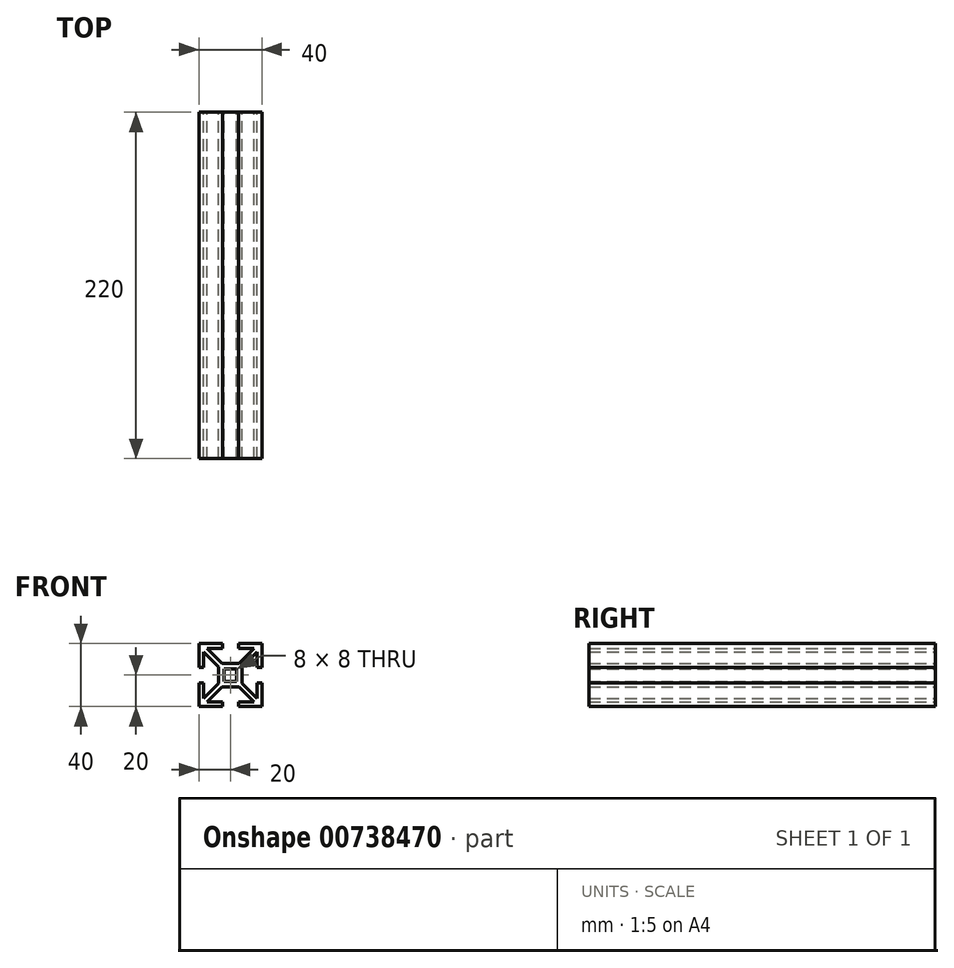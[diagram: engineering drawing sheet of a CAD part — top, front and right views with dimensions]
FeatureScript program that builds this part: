
annotation { "Feature Type Name" : "Feature", "Feature Type Description" : "" }
export const myFeature = defineFeature(function(context is Context, id is Id, definition is map)
    precondition{}
    {
        {
            var Q0;
            Q0=qCreatedBy(makeId("Front.planeOp"),FACE);
            var sketch = newSketch(context, id + "F0", { "sketchPlane" : qUnion([Q0])});
            skPoint(sketch, "E0.middle", {"position": v(0, 0) * mm});
            skLineSegment(sketch, "E1.bottom", {"start": v(20, 20) * mm, "end": v(-20, 20) * mm});
            skLineSegment(sketch, "E1.top", {"start": v(20, -20) * mm, "end": v(-20, -20) * mm});
            skLineSegment(sketch, "E1.left", {"start": v(20, 20) * mm, "end": v(20, -20) * mm});
            skLineSegment(sketch, "E1.right", {"start": v(-20, 20) * mm, "end": v(-20, -20) * mm});
            skLineSegment(sketch, "E2.bottom", {"start": v(4, 4) * mm, "end": v(-4, 4) * mm});
            skLineSegment(sketch, "E2.top", {"start": v(4, -4) * mm, "end": v(-4, -4) * mm});
            skLineSegment(sketch, "E2.left", {"start": v(4, 4) * mm, "end": v(4, -4) * mm});
            skLineSegment(sketch, "E2.right", {"start": v(-4, 4) * mm, "end": v(-4, -4) * mm});
            skLineSegment(sketch, "E3.bottom", {"start": v(7.5, -7.5) * mm, "end": v(-7.5, -7.5) * mm});
            skLineSegment(sketch, "E3.top", {"start": v(7.5, 7.5) * mm, "end": v(-7.5, 7.5) * mm});
            skLineSegment(sketch, "E3.left", {"start": v(7.5, -7.5) * mm, "end": v(7.5, 7.5) * mm});
            skLineSegment(sketch, "E3.right", {"start": v(-7.5, -7.5) * mm, "end": v(-7.5, 7.5) * mm});
            skLineSegment(sketch, "E4", {"start": v(-5, 20) * mm, "end": v(-5, -20) * mm, "construction": true});
            skLineSegment(sketch, "E5", {"start": v(5, -20) * mm, "end": v(5, 20) * mm, "construction": true});
            skLineSegment(sketch, "E6", {"start": v(-20, 5) * mm, "end": v(20, 5) * mm, "construction": true});
            skLineSegment(sketch, "E7", {"start": v(-20, -5) * mm, "end": v(20, -5) * mm, "construction": true});
            skLineSegment(sketch, "E8.bottom", {"start": v(17, 17) * mm, "end": v(-17, 17) * mm});
            skLineSegment(sketch, "E8.top", {"start": v(17, -17) * mm, "end": v(-17, -17) * mm});
            skLineSegment(sketch, "E8.left", {"start": v(17, 17) * mm, "end": v(17, -17) * mm});
            skLineSegment(sketch, "E8.right", {"start": v(-17, 17) * mm, "end": v(-17, -17) * mm});
            skLineSegment(sketch, "E9", {"start": v(0, 0) * mm, "end": v(20, 20) * mm, "construction": true});
            skLineSegment(sketch, "E10", {"start": v(0, 0) * mm, "end": v(20, -20) * mm, "construction": true});
            skLineSegment(sketch, "E11", {"start": v(0, 0) * mm, "end": v(-20, -20) * mm, "construction": true});
            skLineSegment(sketch, "E12", {"start": v(0, 0) * mm, "end": v(-20, 20) * mm, "construction": true});
            skLineSegment(sketch, "E13", {"start": v(5.38, 7.5) * mm, "end": v(14.88, 17) * mm});
            skLineSegment(sketch, "E14", {"start": v(7.5, 5.38) * mm, "end": v(17, 14.88) * mm});
            skLineSegment(sketch, "E15", {"start": v(7.5, -5.38) * mm, "end": v(17, -14.88) * mm});
            skLineSegment(sketch, "E16", {"start": v(5.38, -7.5) * mm, "end": v(14.88, -17) * mm});
            skLineSegment(sketch, "E17", {"start": v(-7.5, -5.38) * mm, "end": v(-17, -14.88) * mm});
            skLineSegment(sketch, "E18", {"start": v(-14.88, -17) * mm, "end": v(-5.38, -7.5) * mm});
            skLineSegment(sketch, "E19", {"start": v(-5.38, 7.5) * mm, "end": v(-14.88, 17) * mm});
            skLineSegment(sketch, "E20", {"start": v(-7.5, 5.38) * mm, "end": v(-17, 14.88) * mm});
            skLineSegment(sketch, "E21", {"start": v(-5, 20) * mm, "end": v(-5, 17) * mm});
            skLineSegment(sketch, "E22", {"start": v(5, 20) * mm, "end": v(5, 17) * mm});
            skLineSegment(sketch, "E23", {"start": v(17, 5) * mm, "end": v(20, 5) * mm});
            skLineSegment(sketch, "E24", {"start": v(17, -5) * mm, "end": v(20, -5) * mm});
            skLineSegment(sketch, "E25", {"start": v(5, -17) * mm, "end": v(5, -20) * mm});
            skLineSegment(sketch, "E26", {"start": v(-5, -17) * mm, "end": v(-5, -20) * mm});
            skLineSegment(sketch, "E27", {"start": v(-17, -5) * mm, "end": v(-20, -5) * mm});
            skLineSegment(sketch, "E28", {"start": v(-17, 5) * mm, "end": v(-20, 5) * mm});
            skSolve(sketch);
        }
        {
            var Q0;
            {var subQ2=sQuery(id+"F0.wireOp",EDGE,"E21");Q0=makeQuery(id+"F0.imprint","IMPRINT",FACE,{"disambiguationData":[TD([[makeQuery(id+"F0.imprint","IMPRINT",EDGE,{"derivedFrom":subQ2}),-1.0]])]});}
            var Q1;
            {var subQ4=sQuery(id+"F0.wireOp",EDGE,"E26");Q1=makeQuery(id+"F0.imprint","IMPRINT",FACE,{"disambiguationData":[TD([[makeQuery(id+"F0.imprint","IMPRINT",EDGE,{"derivedFrom":subQ4}),-1.0]])]});}
            var Q2;
            {var subQ8=sQuery(id+"F0.wireOp",EDGE,"E24");Q2=makeQuery(id+"F0.imprint","IMPRINT",FACE,{"disambiguationData":[TD([[makeQuery(id+"F0.imprint","IMPRINT",EDGE,{"derivedFrom":subQ8}),-1.0]])]});}
            var Q3;
            {var subQ2=sQuery(id+"F0.wireOp",EDGE,"E22");Q3=makeQuery(id+"F0.imprint","IMPRINT",FACE,{"disambiguationData":[TD([[makeQuery(id+"F0.imprint","IMPRINT",EDGE,{"derivedFrom":subQ2}),1.0]])]});}
            var Q4;
            {var subQ4=sQuery(id+"F0.wireOp",EDGE,"E13");Q4=makeQuery(id+"F0.imprint","IMPRINT",FACE,{"disambiguationData":[TD([[makeQuery(id+"F0.imprint","IMPRINT",EDGE,{"derivedFrom":subQ4}),-1.0]])]});}
            var Q5;
            {var subQ4=sQuery(id+"F0.wireOp",EDGE,"E19");Q5=makeQuery(id+"F0.imprint","IMPRINT",FACE,{"disambiguationData":[TD([[makeQuery(id+"F0.imprint","IMPRINT",EDGE,{"derivedFrom":subQ4}),1.0]])]});}
            var Q6;
            {var subQ3=sQuery(id+"F0.wireOp",EDGE,"E17");Q6=makeQuery(id+"F0.imprint","IMPRINT",FACE,{"disambiguationData":[TD([[makeQuery(id+"F0.imprint","IMPRINT",EDGE,{"derivedFrom":subQ3}),1.0]])]});}
            var Q7;
            {var subQ7=sQuery(id+"F0.wireOp",EDGE,"E15");Q7=makeQuery(id+"F0.imprint","IMPRINT",FACE,{"disambiguationData":[TD([[makeQuery(id+"F0.imprint","IMPRINT",EDGE,{"derivedFrom":subQ7}),-1.0]])]});}
            var Q8;
            Q8=makeQuery(id+"F0.imprint","IMPRINT",FACE,{"disambiguationData":[TD([[makeQuery(id+"F0.imprint","IMPRINT",EDGE,{"derivedFrom":sQuery(id+"F0.wireOp",EDGE,"E2.bottom")}),-1.0]])]});
            extrude(context, id + "F1", {"entities" : qUnion([Q0, Q1, Q2, Q3, Q4, Q5, Q6, Q7, Q8]), "endBound" : BoundingType.SYMMETRIC, "depth" : 220 * mm, "offsetDistance" : 25 * mm});
        }
    });
